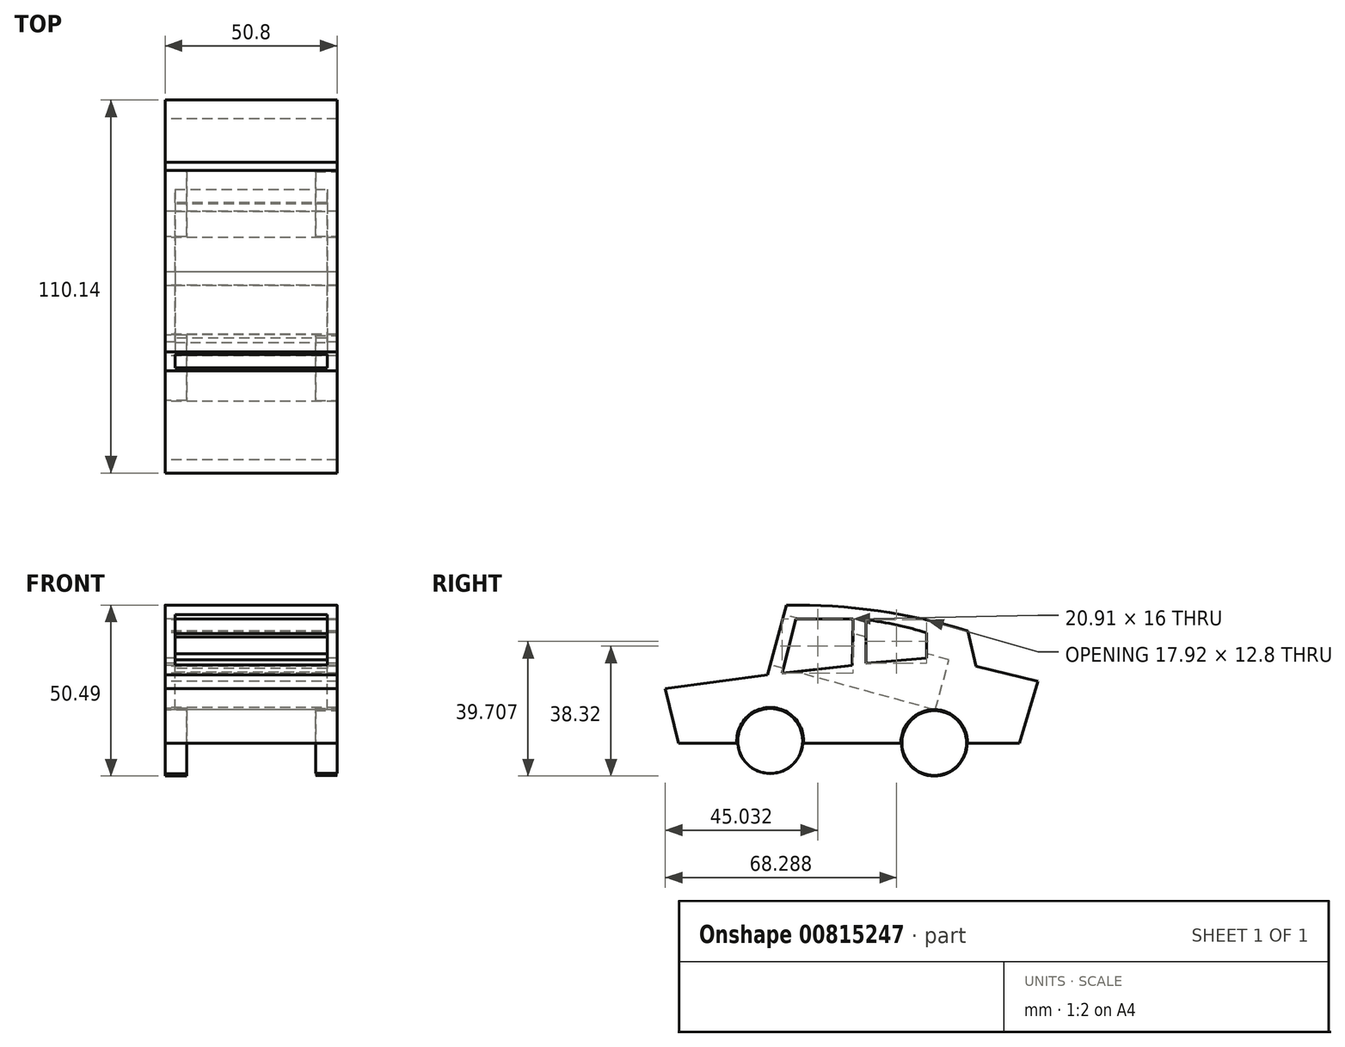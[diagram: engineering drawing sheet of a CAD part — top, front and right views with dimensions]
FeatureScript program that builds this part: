
annotation { "Feature Type Name" : "Feature", "Feature Type Description" : "" }
export const myFeature = defineFeature(function(context is Context, id is Id, definition is map)
    precondition{}
    {
        {
            var Q0;
            Q0=qCreatedBy(makeId("Right.planeOp"),FACE);
            var sketch = newSketch(context, id + "F0", { "sketchPlane" : qUnion([Q0])});
            skLineSegment(sketch, "E0", {"start": v(-49.53, 0) * mm, "end": v(-53.46, 16.04) * mm});
            skLineSegment(sketch, "E1", {"start": v(-53.46, 16.04) * mm, "end": v(-23.26, 20.15) * mm});
            skLineSegment(sketch, "E2", {"start": v(-23.26, 20.15) * mm, "end": v(-17.65, 40.74) * mm});
            skArc(sketch, "E3", {"start": v(35.87, 33.1) * mm, "mid": v(9.41, 39.02) * mm, "end": v(-17.65, 40.74) * mm});
            skLineSegment(sketch, "E4", {"start": v(35.87, 33.1) * mm, "end": v(38.31, 22.7) * mm});
            skLineSegment(sketch, "E5", {"start": v(38.31, 22.7) * mm, "end": v(56.68, 18.22) * mm});
            skLineSegment(sketch, "E6", {"start": v(56.68, 18.22) * mm, "end": v(51.13, 0) * mm});
            skLineSegment(sketch, "E7", {"start": v(51.13, 0) * mm, "end": v(35.87, 0) * mm});
            skArc(sketch, "E8", {"start": v(35.87, 0) * mm, "mid": v(26, 9.87) * mm, "end": v(16.12, 0) * mm});
            skLineSegment(sketch, "E9", {"start": v(16.12, 0) * mm, "end": v(-12.58, 0) * mm});
            skArc(sketch, "E10", {"start": v(-12.58, 0) * mm, "mid": v(-22.46, 10.52) * mm, "end": v(-32.33, 0) * mm});
            skLineSegment(sketch, "E11", {"start": v(-49.53, 0) * mm, "end": v(-32.33, 0) * mm});
            skSolve(sketch);
        }
        {
            var Q0;
            Q0=makeQuery(id+"F0.imprint","IMPRINT",FACE,{"disambiguationData":[TD([[makeQuery(id+"F0.imprint","IMPRINT",EDGE,{"derivedFrom":sQuery(id+"F0.wireOp",EDGE,"E0")}),-1.0]])]});
            extrude(context, id + "F1", {"entities" : qUnion([Q0]), "endBound" : BoundingType.SYMMETRIC, "depth" : 50.8 * mm, "offsetDistance" : 25.4 * mm});
        }
        {
            var Q0;
            Q0=makeQuery(id+"F1.opExtrude","CAP_FACE",FACE,{"disambiguationData":[OSD([sQuery(id+"F0.wireOp",EDGE,"E0"),sQuery(id+"F0.wireOp",EDGE,"E1"),sQuery(id+"F0.wireOp",EDGE,"E2"),sQuery(id+"F0.wireOp",EDGE,"E3"),sQuery(id+"F0.wireOp",EDGE,"E4"),sQuery(id+"F0.wireOp",EDGE,"E5"),sQuery(id+"F0.wireOp",EDGE,"E6"),sQuery(id+"F0.wireOp",EDGE,"E7"),sQuery(id+"F0.wireOp",EDGE,"E8"),sQuery(id+"F0.wireOp",EDGE,"E9"),sQuery(id+"F0.wireOp",EDGE,"E10"),sQuery(id+"F0.wireOp",EDGE,"E11")])],"isStart":false});
            var sketch = newSketch(context, id + "F2", { "sketchPlane" : qUnion([Q0])});
            skCircle(sketch, "E12", {"center": v(-22.46, 0.62) * mm, "radius": 9.56 * mm});
            skCircle(sketch, "E13", {"center": v(26, 0) * mm, "radius": 9.54 * mm});
            skSolve(sketch);
        }
        {
            var Q0;
            Q0 = qSketchRegion(id + "F2", true);
            extrude(context, id + "F3", {"entities" : qUnion([Q0]), "oppositeDirection" : true, "depth" : 6.35 * mm, "offsetDistance" : 25.4 * mm});
        }
        {
            var Q0;
            Q0=makeQuery(id+"F1.opExtrude","CAP_FACE",FACE,{"disambiguationData":[OSD([sQuery(id+"F0.wireOp",EDGE,"E0"),sQuery(id+"F0.wireOp",EDGE,"E1"),sQuery(id+"F0.wireOp",EDGE,"E2"),sQuery(id+"F0.wireOp",EDGE,"E3"),sQuery(id+"F0.wireOp",EDGE,"E4"),sQuery(id+"F0.wireOp",EDGE,"E5"),sQuery(id+"F0.wireOp",EDGE,"E6"),sQuery(id+"F0.wireOp",EDGE,"E7"),sQuery(id+"F0.wireOp",EDGE,"E8"),sQuery(id+"F0.wireOp",EDGE,"E9"),sQuery(id+"F0.wireOp",EDGE,"E10"),sQuery(id+"F0.wireOp",EDGE,"E11")])],"isStart":true});
            var sketch = newSketch(context, id + "F4", { "sketchPlane" : qUnion([Q0])});
            skCircle(sketch, "E14", {"center": v(-26, 0) * mm, "radius": 9.73 * mm});
            skCircle(sketch, "E15", {"center": v(22.46, 0.62) * mm, "radius": 9.66 * mm});
            skSolve(sketch);
        }
        {
            var Q0;
            Q0 = qSketchRegion(id + "F4", true);
            extrude(context, id + "F5", {"entities" : qUnion([Q0]), "oppositeDirection" : true, "depth" : 6.35 * mm, "offsetDistance" : 25.4 * mm});
        }
        {
            var Q0;
            Q0=makeQuery(id+"F1.opExtrude","SWEPT_FACE",FACE,{"disambiguationData":[OSD([sQuery(id+"F0.wireOp",EDGE,"E2")])]});
            var sketch = newSketch(context, id + "F6", { "sketchPlane" : qUnion([Q0])});
            skLineSegment(sketch, "E16.bottom", {"start": v(-22.5, 16.37) * mm, "end": v(22.5, 16.37) * mm});
            skLineSegment(sketch, "E16.top", {"start": v(-22.5, 31.7) * mm, "end": v(22.5, 31.7) * mm});
            skLineSegment(sketch, "E16.left", {"start": v(-22.5, 16.37) * mm, "end": v(-22.5, 31.7) * mm});
            skLineSegment(sketch, "E16.right", {"start": v(22.5, 16.37) * mm, "end": v(22.5, 31.7) * mm});
            skSolve(sketch);
        }
        {
            var Q0;
            Q0 = qSketchRegion(id + "F6", true);
            extrude(context, id + "F7", {"entities" : qUnion([Q0]), "operationType" : NewBodyOperationType.REMOVE, "oppositeDirection" : true, "depth" : 50.55 * mm, "offsetDistance" : 25.4 * mm});
        }
        {
            var Q0;
            Q0=makeQuery(id+"F1.opExtrude","CAP_FACE",FACE,{"disambiguationData":[OSD([sQuery(id+"F0.wireOp",EDGE,"E0"),sQuery(id+"F0.wireOp",EDGE,"E1"),sQuery(id+"F0.wireOp",EDGE,"E2"),sQuery(id+"F0.wireOp",EDGE,"E3"),sQuery(id+"F0.wireOp",EDGE,"E4"),sQuery(id+"F0.wireOp",EDGE,"E5"),sQuery(id+"F0.wireOp",EDGE,"E6"),sQuery(id+"F0.wireOp",EDGE,"E7"),sQuery(id+"F0.wireOp",EDGE,"E8"),sQuery(id+"F0.wireOp",EDGE,"E9"),sQuery(id+"F0.wireOp",EDGE,"E10"),sQuery(id+"F0.wireOp",EDGE,"E11")])],"isStart":true});
            var sketch = newSketch(context, id + "F8", { "sketchPlane" : qUnion([Q0])});
            skLineSegment(sketch, "E17", {"start": v(-1.81, 22.94) * mm, "end": v(18.88, 20.59) * mm});
            skLineSegment(sketch, "E18", {"start": v(18.88, 20.59) * mm, "end": v(14.83, 36.6) * mm});
            skLineSegment(sketch, "E19", {"start": v(14.83, 36.6) * mm, "end": v(-2.03, 36.6) * mm});
            skLineSegment(sketch, "E20", {"start": v(-2.03, 36.6) * mm, "end": v(-1.81, 22.94) * mm});
            skLineSegment(sketch, "E21", {"start": v(-5.87, 23.58) * mm, "end": v(-5.87, 36.38) * mm});
            skArc(sketch, "E22", {"start": v(-5.87, 36.38) * mm, "mid": v(-14.91, 34.86) * mm, "end": v(-23.79, 32.54) * mm});
            skLineSegment(sketch, "E23", {"start": v(-23.79, 32.54) * mm, "end": v(-23.79, 25.07) * mm});
            skLineSegment(sketch, "E24", {"start": v(-23.79, 25.07) * mm, "end": v(-5.87, 23.58) * mm});
            skSolve(sketch);
        }
        {
            var Q0;
            Q0 = qSketchRegion(id + "F8", true);
            extrude(context, id + "F9", {"entities" : qUnion([Q0]), "operationType" : NewBodyOperationType.REMOVE, "oppositeDirection" : true, "depth" : 59.69 * mm, "offsetDistance" : 25.4 * mm});
        }
    });
